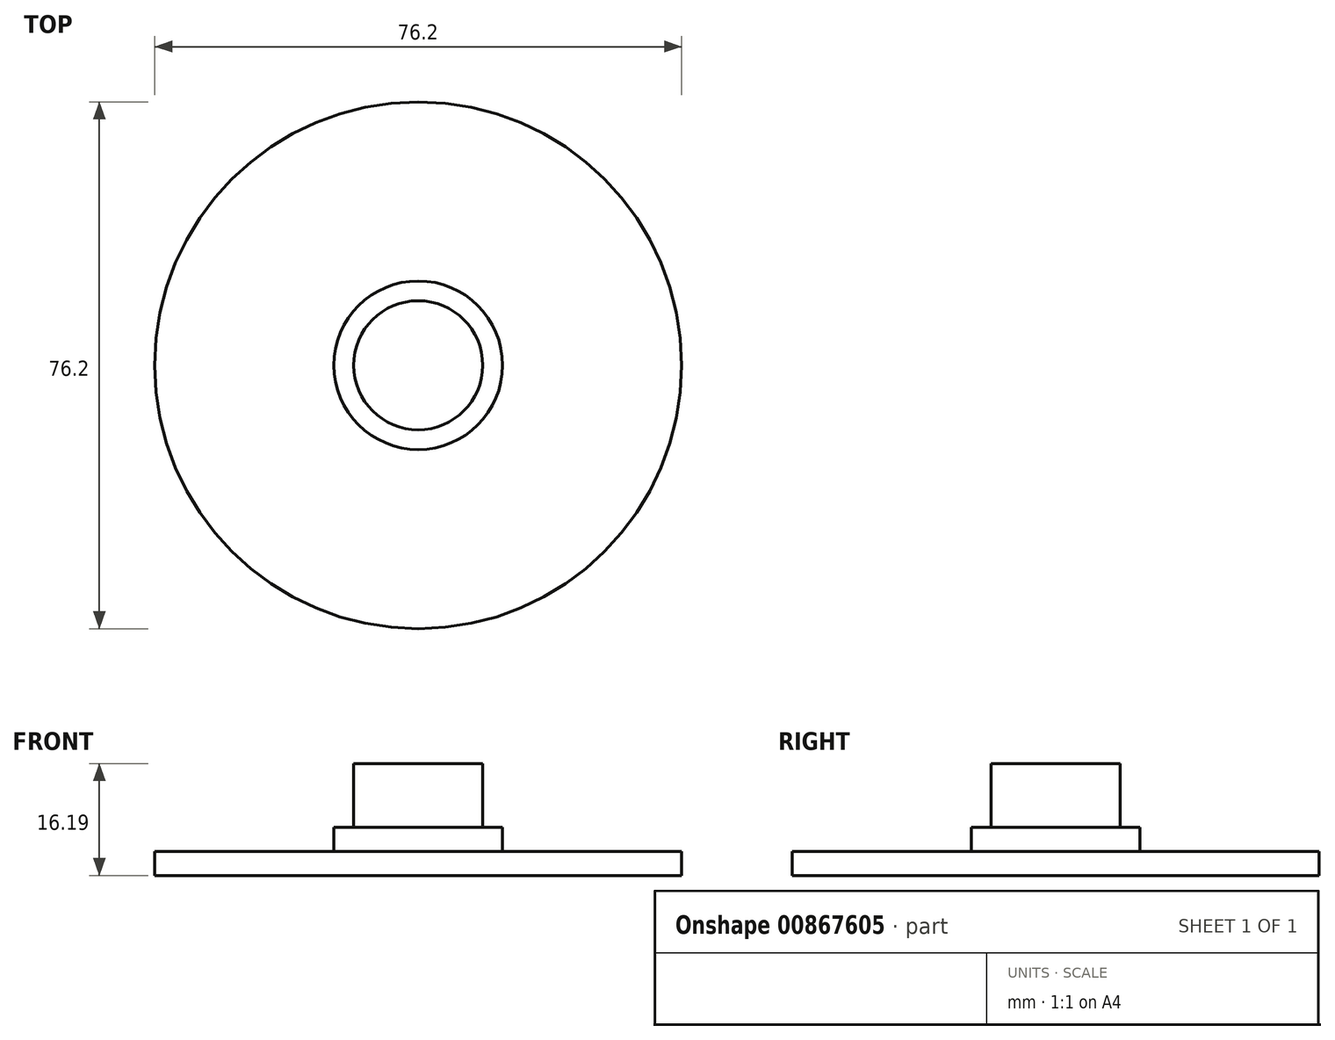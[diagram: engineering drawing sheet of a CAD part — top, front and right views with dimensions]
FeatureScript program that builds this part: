
annotation { "Feature Type Name" : "Feature", "Feature Type Description" : "" }
export const myFeature = defineFeature(function(context is Context, id is Id, definition is map)
    precondition{}
    {
        {
            var Q0;
            Q0=qCreatedBy(makeId("Top.planeOp"),FACE);
            var sketch = newSketch(context, id + "F0", { "sketchPlane" : qUnion([Q0])});
            skCircle(sketch, "E0", {"center": v(0, 0) * mm, "radius": 12.2 * mm});
            skCircle(sketch, "E1", {"center": v(0, 0) * mm, "radius": 9.33 * mm});
            skCircle(sketch, "E2", {"center": v(0, 0) * mm, "radius": 38.1 * mm});
            skSolve(sketch);
        }
        {
            var Q0;
            Q0=makeQuery(id+"F0.imprint","IMPRINT",FACE,{"disambiguationData":[TD([[makeQuery(id+"F0.imprint","IMPRINT",EDGE,{"derivedFrom":sQuery(id+"F0.wireOp",EDGE,"E0")}),1.0]])]});
            extrude(context, id + "F1", {"entities" : qUnion([Q0]), "depth" : 3.5 * mm, "offsetDistance" : 25.4 * mm});
        }
        {
            var Q0;
            Q0=makeQuery(id+"F0.imprint","IMPRINT",FACE,{"disambiguationData":[TD([[makeQuery(id+"F0.imprint","IMPRINT",EDGE,{"derivedFrom":sQuery(id+"F0.wireOp",EDGE,"E1")}),1.0]])]});
            extrude(context, id + "F2", {"entities" : qUnion([Q0]), "operationType" : NewBodyOperationType.ADD, "depth" : 12.7 * mm, "offsetDistance" : 25.4 * mm});
        }
        {
            var Q0;
            Q0=makeQuery(id+"F0.imprint","IMPRINT",FACE,{"disambiguationData":[TD([[makeQuery(id+"F0.imprint","IMPRINT",EDGE,{"derivedFrom":sQuery(id+"F0.wireOp",EDGE,"E0")}),-1.0]])]});
            var Q1;
            Q1=makeQuery(id+"F0.imprint","IMPRINT",FACE,{"disambiguationData":[TD([[makeQuery(id+"F0.imprint","IMPRINT",EDGE,{"derivedFrom":sQuery(id+"F0.wireOp",EDGE,"E1")}),1.0]])]});
            var Q2;
            Q2=makeQuery(id+"F0.imprint","IMPRINT",FACE,{"disambiguationData":[TD([[makeQuery(id+"F0.imprint","IMPRINT",EDGE,{"derivedFrom":sQuery(id+"F0.wireOp",EDGE,"E0")}),1.0]])]});
            extrude(context, id + "F3", {"entities" : qUnion([Q0, Q1, Q2]), "operationType" : NewBodyOperationType.ADD, "depth" : -3.5 * mm, "offsetDistance" : 25.4 * mm});
        }
    });
